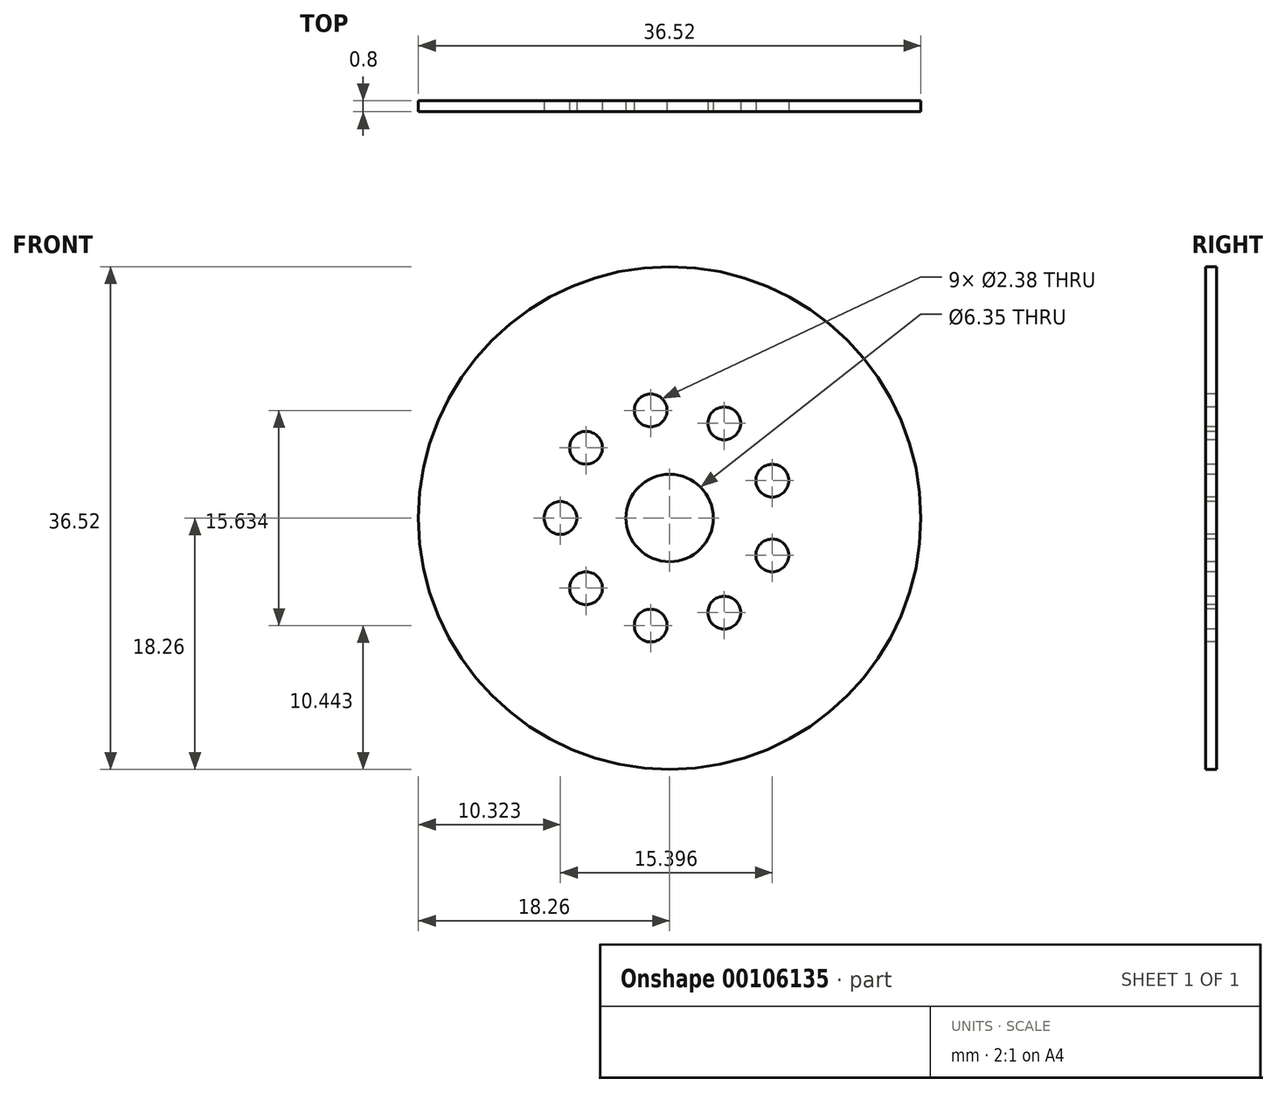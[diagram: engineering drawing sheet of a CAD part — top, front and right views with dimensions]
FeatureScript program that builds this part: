
annotation { "Feature Type Name" : "Feature", "Feature Type Description" : "" }
export const myFeature = defineFeature(function(context is Context, id is Id, definition is map)
    precondition{}
    {
        {
            var Q0;
            Q0=qCreatedBy(makeId("Right.planeOp"),FACE);
            var sketch = newSketch(context, id + "F0", { "sketchPlane" : qUnion([Q0])});
            skLineSegment(sketch, "E0", {"start": v(0, 0) * mm, "end": v(-117.48, 0) * mm, "construction": true});
            skLineSegment(sketch, "E1.bottom", {"start": v(-117.48, 0) * mm, "end": v(-118.27, 0) * mm});
            skLineSegment(sketch, "E1.top", {"start": v(-117.48, 18.26) * mm, "end": v(-118.27, 18.26) * mm});
            skLineSegment(sketch, "E1.left", {"start": v(-117.48, 0) * mm, "end": v(-117.48, 18.26) * mm});
            skLineSegment(sketch, "E1.right", {"start": v(-118.27, 0) * mm, "end": v(-118.27, 18.26) * mm});
            skSolve(sketch);
        }
        {
            var Q0;
            Q0 = qSketchRegion(id + "F0", true);
            var Q1;
            Q1=sQuery(id+"F0.wireOp",EDGE,"E0");
            revolve(context, id + "F1", {"entities" : qUnion([Q0]), "axis" : qUnion([Q1]), "revolveType" : RevolveType.FULL});
        }
        {
            var Q0;
            Q0=makeQuery(id+"F1.opRevolve","SWEPT_FACE",FACE,{"disambiguationData":[OSD([sQuery(id+"F0.wireOp",EDGE,"E1.right")])]});
            var sketch = newSketch(context, id + "F2", { "sketchPlane" : qUnion([Q0])});
            skLineSegment(sketch, "E2", {"start": v(0, 0) * mm, "end": v(-7.94, 0) * mm, "construction": true});
            skCircle(sketch, "E3", {"center": v(0, 0) * mm, "radius": 3.18 * mm});
            skCircle(sketch, "E4", {"center": v(-7.94, 0) * mm, "radius": 1.2 * mm});
            skCircle(sketch, "E5.1.0", {"center": v(-6.08, -5.1) * mm, "radius": 1.2 * mm});
            skCircle(sketch, "E5.2.0", {"center": v(-1.38, -7.82) * mm, "radius": 1.2 * mm});
            skCircle(sketch, "E5.3.0", {"center": v(3.97, -6.87) * mm, "radius": 1.2 * mm});
            skCircle(sketch, "E5.4.0", {"center": v(7.46, -2.71) * mm, "radius": 1.2 * mm});
            skCircle(sketch, "E5.5.0", {"center": v(7.46, 2.71) * mm, "radius": 1.2 * mm});
            skCircle(sketch, "E5.6.0", {"center": v(3.97, 6.87) * mm, "radius": 1.2 * mm});
            skCircle(sketch, "E5.7.0", {"center": v(-1.38, 7.82) * mm, "radius": 1.2 * mm});
            skCircle(sketch, "E5.8.0", {"center": v(-6.08, 5.1) * mm, "radius": 1.2 * mm});
            skSolve(sketch);
        }
        {
            var Q0;
            Q0 = qSketchRegion(id + "F2", true);
            extrude(context, id + "F3", {"entities" : qUnion([Q0]), "operationType" : NewBodyOperationType.REMOVE, "endBound" : BoundingType.UP_TO_NEXT, "oppositeDirection" : true, "depth" : 25.4 * mm});
        }
    });
